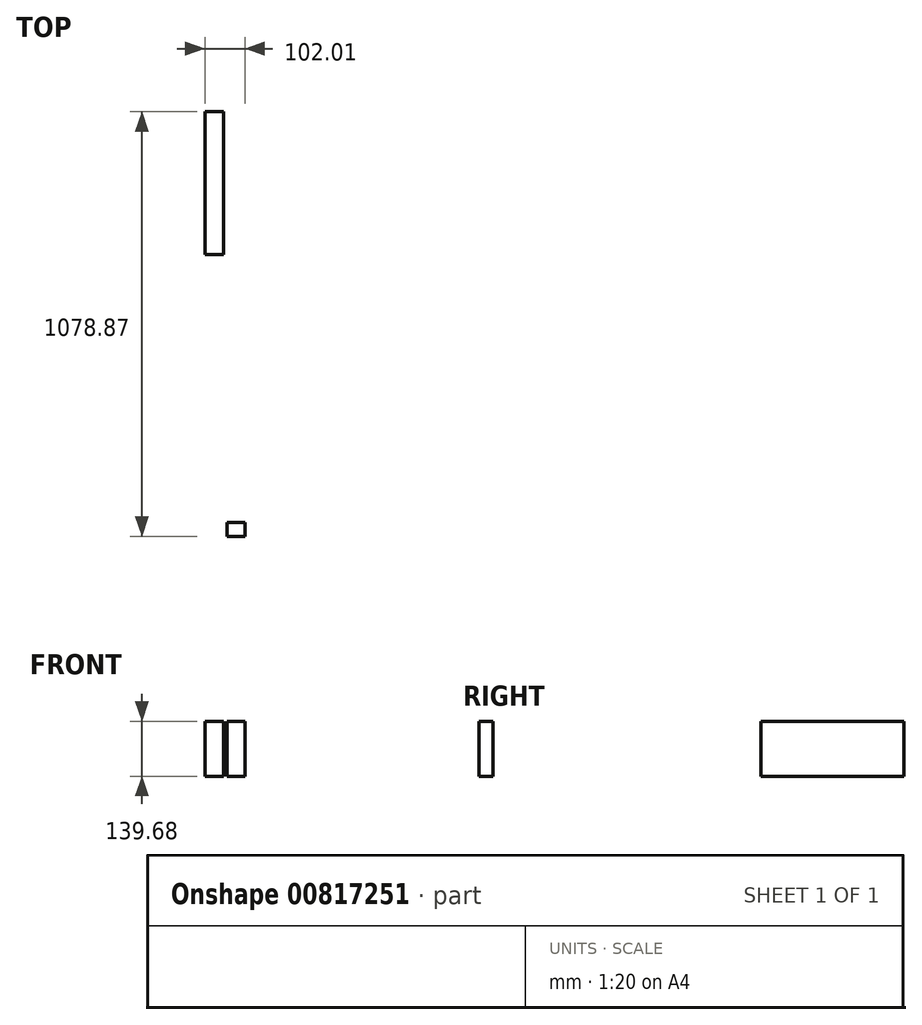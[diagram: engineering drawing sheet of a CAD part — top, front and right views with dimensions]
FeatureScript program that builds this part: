
annotation { "Feature Type Name" : "Feature", "Feature Type Description" : "" }
export const myFeature = defineFeature(function(context is Context, id is Id, definition is map)
    precondition{}
    {
        {
            var Q0;
            Q0=qCreatedBy(makeId("Top.planeOp"),FACE);
            var sketch = newSketch(context, id + "F0", { "sketchPlane" : qUnion([Q0])});
            skLineSegment(sketch, "E0.bottom", {"start": v(-54.26, 1044.12) * mm, "end": v(-102, 1044.12) * mm});
            skLineSegment(sketch, "E0.top", {"start": v(-54.26, 681.57) * mm, "end": v(-102, 681.57) * mm});
            skLineSegment(sketch, "E0.left", {"start": v(-54.26, 1044.12) * mm, "end": v(-54.26, 681.57) * mm});
            skLineSegment(sketch, "E0.right", {"start": v(-102, 1044.12) * mm, "end": v(-102, 681.57) * mm});
            skLineSegment(sketch, "E1.bottom", {"start": v(-45, 0) * mm, "end": v(0, 0) * mm});
            skLineSegment(sketch, "E1.top", {"start": v(-45, -34.75) * mm, "end": v(0, -34.75) * mm});
            skLineSegment(sketch, "E1.left", {"start": v(-45, 0) * mm, "end": v(-45, -34.75) * mm});
            skLineSegment(sketch, "E1.right", {"start": v(0, 0) * mm, "end": v(0, -34.75) * mm});
            skSolve(sketch);
        }
        {
            var Q0;
            Q0 = qSketchRegion(id + "F0", true);
            extrude(context, id + "F1", {"entities" : qUnion([Q0]), "depth" : 139.68 * mm, "offsetDistance" : 25.4 * mm});
        }
    });
